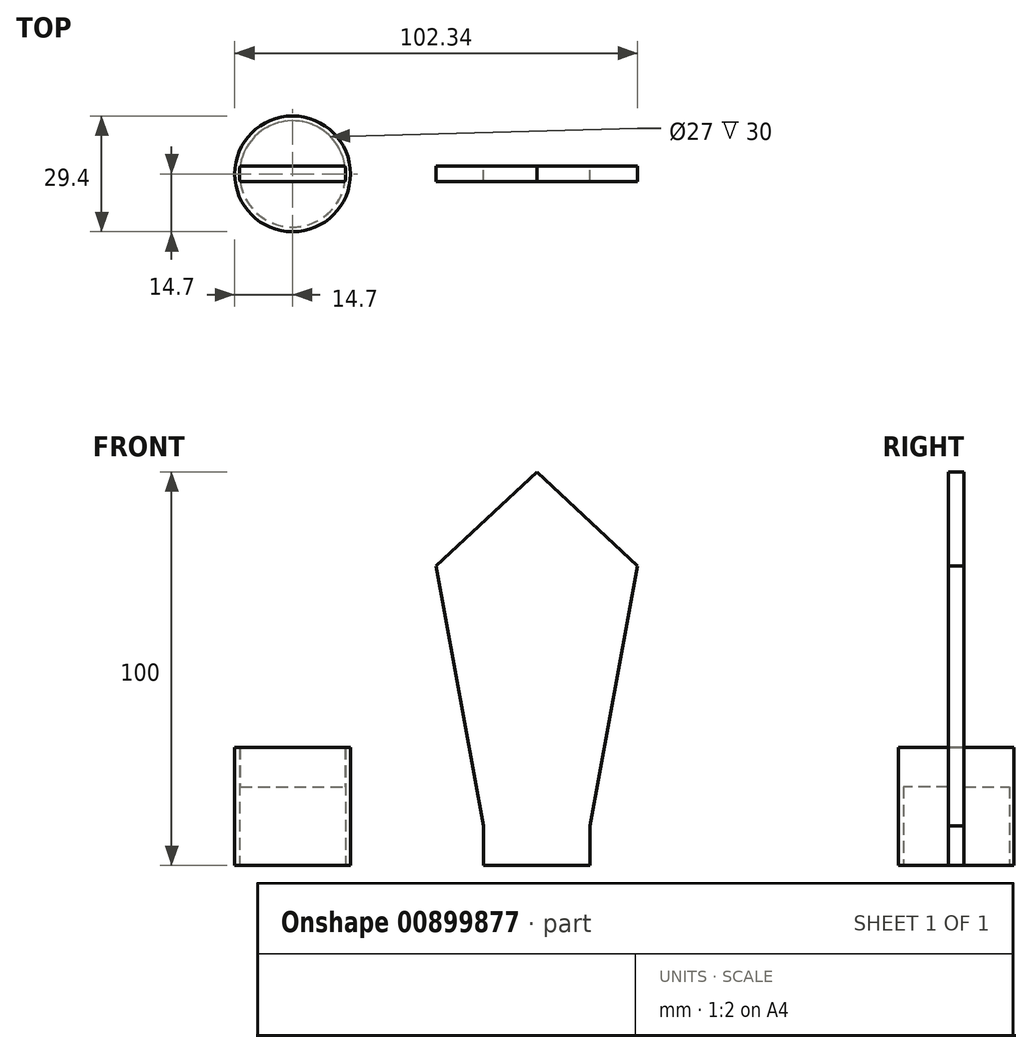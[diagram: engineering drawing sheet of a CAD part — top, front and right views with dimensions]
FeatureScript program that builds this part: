
annotation { "Feature Type Name" : "Feature", "Feature Type Description" : "" }
export const myFeature = defineFeature(function(context is Context, id is Id, definition is map)
    precondition{}
    {
        {
            var Q0;
            Q0=qCreatedBy(makeId("Top.planeOp"),FACE);
            var sketch = newSketch(context, id + "F0", { "sketchPlane" : qUnion([Q0])});
            skCircle(sketch, "E0", {"center": v(0, 0) * mm, "radius": 13.5 * mm});
            skCircle(sketch, "E1", {"center": v(0, 0) * mm, "radius": 14.7 * mm});
            skLineSegment(sketch, "E2", {"start": v(-13.5, 0) * mm, "end": v(13.5, 0) * mm});
            skLineSegment(sketch, "E3.bottom", {"start": v(-13.35, 2) * mm, "end": v(13.35, 2) * mm});
            skLineSegment(sketch, "E3.top", {"start": v(-13.35, -2) * mm, "end": v(13.35, -2) * mm});
            skLineSegment(sketch, "E3.left", {"start": v(-13.35, 2) * mm, "end": v(-13.35, -2) * mm});
            skLineSegment(sketch, "E3.right", {"start": v(13.35, 2) * mm, "end": v(13.35, -2) * mm});
            skSolve(sketch);
        }
        {
            var Q0;
            Q0 = qSketchRegion(id + "F0", true);
            extrude(context, id + "F1", {"entities" : qUnion([Q0]), "depth" : 30 * mm, "offsetDistance" : 25 * mm});
        }
        {
            var Q0;
            {var subQ0=sQuery(id+"F0.wireOp",EDGE,"E3.bottom");Q0=makeQuery(id+"F0.imprint","IMPRINT",FACE,{"disambiguationData":[TD([[makeQuery(id+"F0.imprint","IMPRINT",EDGE,{"derivedFrom":subQ0}),1.0]])]});}
            var Q1;
            {var subQ0=sQuery(id+"F0.wireOp",EDGE,"E3.top");Q1=makeQuery(id+"F0.imprint","IMPRINT",FACE,{"disambiguationData":[TD([[makeQuery(id+"F0.imprint","IMPRINT",EDGE,{"derivedFrom":subQ0}),-1.0]])]});}
            extrude(context, id + "F2", {"entities" : qUnion([Q0, Q1]), "operationType" : NewBodyOperationType.ADD, "depth" : 30 * mm, "offsetDistance" : 25 * mm, "hasSecondDirection" : true, "secondDirectionOppositeDirection" : false, "secondDirectionDepth" : 20 * mm});
        }
        {
            var Q0;
            Q0=qCreatedBy(makeId("Front.planeOp"),FACE);
            var sketch = newSketch(context, id + "F3", { "sketchPlane" : qUnion([Q0])});
            skLineSegment(sketch, "E4", {"start": v(75.53, 0) * mm, "end": v(48.53, 0) * mm});
            skLineSegment(sketch, "E5", {"start": v(48.53, 0) * mm, "end": v(48.53, 10) * mm});
            skLineSegment(sketch, "E6", {"start": v(48.53, 10) * mm, "end": v(75.53, 10) * mm});
            skLineSegment(sketch, "E7", {"start": v(75.53, 10) * mm, "end": v(75.53, 0) * mm});
            skLineSegment(sketch, "E8", {"start": v(62.03, 0) * mm, "end": v(62.03, 100) * mm});
            skLineSegment(sketch, "E9", {"start": v(62.03, 100) * mm, "end": v(87.64, 76.15) * mm});
            skLineSegment(sketch, "E10", {"start": v(75.53, 10) * mm, "end": v(87.64, 76.15) * mm});
            skLineSegment(sketch, "E11.MirrorCS", {"start": v(62.03, 100) * mm, "end": v(36.42, 76.15) * mm});
            skLineSegment(sketch, "E12.MirrorCS", {"start": v(48.53, 10) * mm, "end": v(36.42, 76.15) * mm});
            skSolve(sketch);
        }
        {
            var Q0;
            {var subQ4=sQuery(id+"F3.wireOp",EDGE,"E9");Q0=makeQuery(id+"F3.imprint","IMPRINT",FACE,{"disambiguationData":[TD([[makeQuery(id+"F3.imprint","IMPRINT",EDGE,{"derivedFrom":subQ4}),-1.0]])]});}
            var Q1;
            {var subQ4=sQuery(id+"F3.wireOp",EDGE,"E11.MirrorCS");Q1=makeQuery(id+"F3.imprint","IMPRINT",FACE,{"disambiguationData":[TD([[makeQuery(id+"F3.imprint","IMPRINT",EDGE,{"derivedFrom":subQ4}),1.0]])]});}
            var Q2;
            {var subQ0=sQuery(id+"F3.wireOp",EDGE,"E5");Q2=makeQuery(id+"F3.imprint","IMPRINT",FACE,{"disambiguationData":[TD([[makeQuery(id+"F3.imprint","IMPRINT",EDGE,{"derivedFrom":subQ0}),-1.0]])]});}
            var Q3;
            {var subQ0=sQuery(id+"F3.wireOp",EDGE,"E7");Q3=makeQuery(id+"F3.imprint","IMPRINT",FACE,{"disambiguationData":[TD([[makeQuery(id+"F3.imprint","IMPRINT",EDGE,{"derivedFrom":subQ0}),-1.0]])]});}
            extrude(context, id + "F4", {"entities" : qUnion([Q0, Q1, Q2, Q3]), "depth" : 2 * mm, "offsetDistance" : 25 * mm, "hasSecondDirection" : true, "secondDirectionOppositeDirection" : true, "secondDirectionDepth" : 2 * mm});
        }
    });
